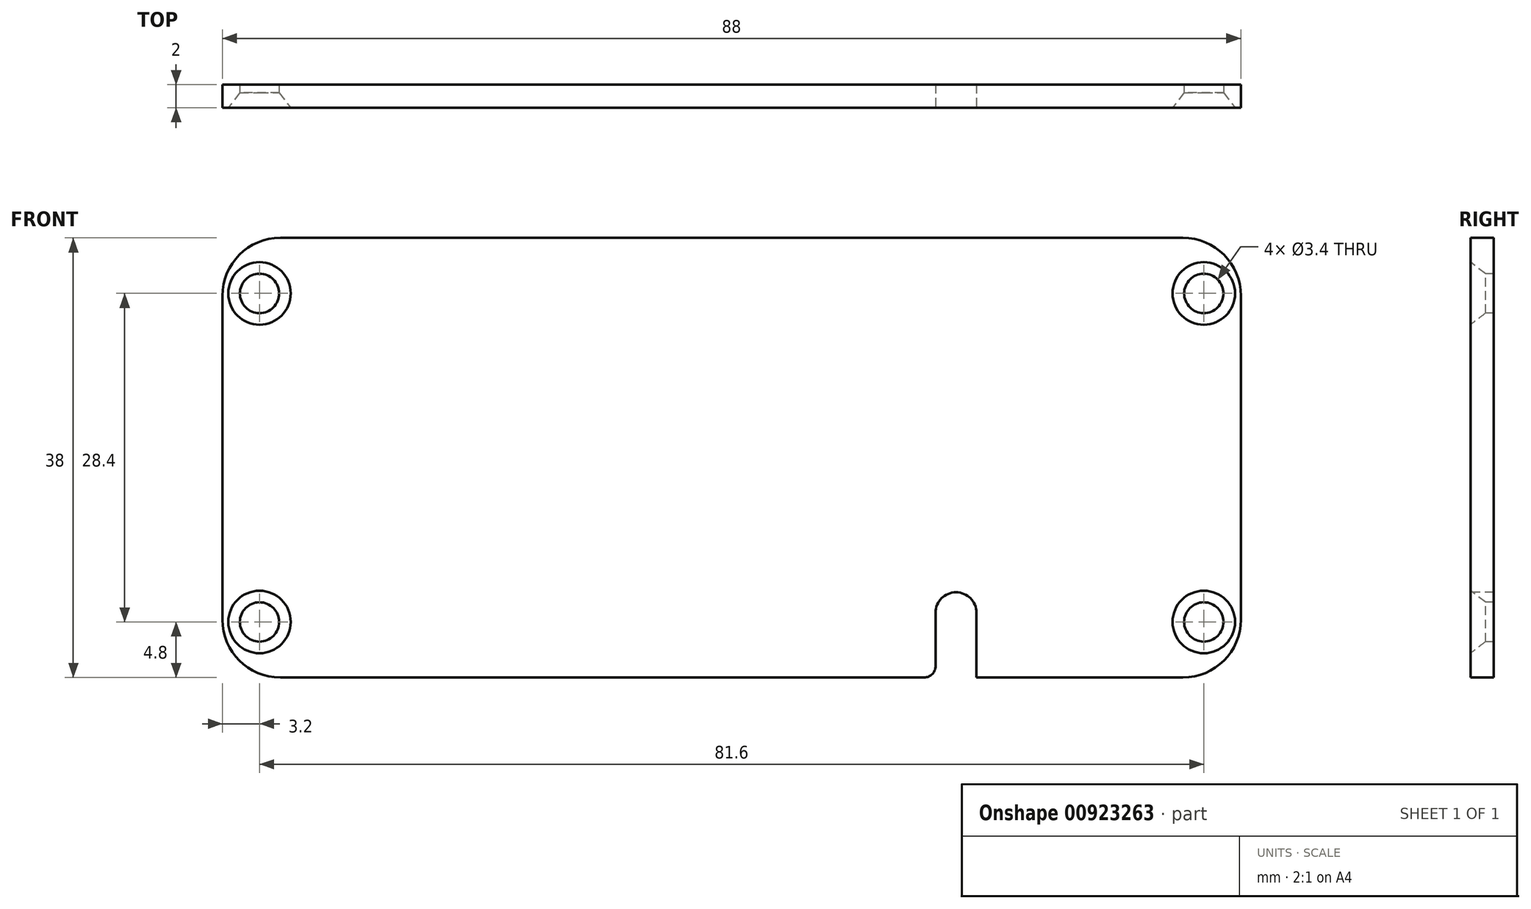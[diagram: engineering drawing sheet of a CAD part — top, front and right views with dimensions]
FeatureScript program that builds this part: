
annotation { "Feature Type Name" : "Feature", "Feature Type Description" : "" }
export const myFeature = defineFeature(function(context is Context, id is Id, definition is map)
    precondition{}
    {
        {
            var Q0;
            Q0=qCreatedBy(makeId("Front.planeOp"),FACE);
            var sketch = newSketch(context, id + "F0", { "sketchPlane" : qUnion([Q0])});
            skLineSegment(sketch, "E0.bottom", {"start": v(-88, 38) * mm, "end": v(0, 38) * mm});
            skLineSegment(sketch, "E0.top", {"start": v(-88, 0) * mm, "end": v(0, 0) * mm});
            skLineSegment(sketch, "E0.left", {"start": v(-88, 38) * mm, "end": v(-88, 0) * mm});
            skLineSegment(sketch, "E0.right", {"start": v(0, 38) * mm, "end": v(0, 0) * mm});
            skCircle(sketch, "E1", {"center": v(-84.8, 33.2) * mm, "radius": 1.7 * mm});
            skLineSegment(sketch, "E2", {"start": v(-84.8, 31.5) * mm, "end": v(-84.8, 6.5) * mm, "construction": true});
            skLineSegment(sketch, "E3", {"start": v(-84.8, 19) * mm, "end": v(0, 19) * mm, "construction": true});
            skCircle(sketch, "E4", {"center": v(-84.8, 4.8) * mm, "radius": 1.7 * mm});
            skLineSegment(sketch, "E5", {"start": v(-44, 38) * mm, "end": v(-44, 0) * mm, "construction": true});
            skCircle(sketch, "E6.MirrorC", {"center": v(-3.2, 33.2) * mm, "radius": 1.7 * mm});
            skLineSegment(sketch, "E7.MirrorCS", {"start": v(-3.2, 31.5) * mm, "end": v(-3.2, 6.5) * mm, "construction": true});
            skCircle(sketch, "E8.MirrorC", {"center": v(-3.2, 4.8) * mm, "radius": 1.7 * mm});
            skPoint(sketch, "E9.middle", {"position": v(-44, 19) * mm});
            skPoint(sketch, "E10.middle", {"position": v(-44, 7.78) * mm});
            skLineSegment(sketch, "E11", {"start": v(-26.38, 0) * mm, "end": v(-26.38, 5.6) * mm});
            skArc(sketch, "E12", {"start": v(-22.85, 5.6) * mm, "mid": v(-24.61, 7.36) * mm, "end": v(-26.38, 5.6) * mm});
            skLineSegment(sketch, "E13", {"start": v(-22.85, 5.6) * mm, "end": v(-22.85, 0) * mm});
            skSolve(sketch);
        }
        {
            var Q0;
            Q0=qSketchRegion(id+"F0",true);
            extrude(context, id + "F1", {"entities" : qUnion([Q0]), "oppositeDirection" : true, "depth" : 2 * mm, "offsetDistance" : 25 * mm});
        }
        {
            var Q0;
            Q0=makeQuery(id+"F1.opExtrude","SWEPT_EDGE",EDGE,{"disambiguationData":[OSD([sQuery(id+"F0.wireOp",EDGE,"E0.bottom"),sQuery(id+"F0.wireOp",EDGE,"E0.left")])]});
            var Q1;
            Q1=makeQuery(id+"F1.opExtrude","SWEPT_EDGE",EDGE,{"disambiguationData":[OSD([sQuery(id+"F0.wireOp",EDGE,"E0.top"),sQuery(id+"F0.wireOp",EDGE,"E0.left")])]});
            var Q2;
            Q2=makeQuery(id+"F1.opExtrude","SWEPT_EDGE",EDGE,{"disambiguationData":[OSD([sQuery(id+"F0.wireOp",EDGE,"E0.top"),sQuery(id+"F0.wireOp",EDGE,"E0.right")])]});
            var Q3;
            Q3=makeQuery(id+"F1.opExtrude","SWEPT_EDGE",EDGE,{"disambiguationData":[OSD([sQuery(id+"F0.wireOp",EDGE,"E0.bottom"),sQuery(id+"F0.wireOp",EDGE,"E0.right")])]});
            fillet(context, id + "F2", {"entities" : qUnion([Q0, Q1, Q2, Q3]), "radius" : 5 * mm, "tangentPropagation" : true, "allowEdgeOverflow" : false});
        }
        {
            var Q0;
            Q0=sQuery(id+"F0.wireOp",VERTEX,"E4.center");
            var Q1;
            Q1=sQuery(id+"F0.wireOp",VERTEX,"E1.center");
            var Q2;
            Q2=sQuery(id+"F0.wireOp",VERTEX,"E8.MirrorC.center");
            var Q3;
            Q3=sQuery(id+"F0.wireOp",VERTEX,"E6.MirrorC.center");
            var Q4;
            Q4=makeQuery(id+"F1.opExtrude","SWEPT_BODY",BODY,{"disambiguationData":[OSD([sQuery(id+"F0.wireOp",EDGE,"E0.bottom"),sQuery(id+"F0.wireOp",EDGE,"E0.top"),sQuery(id+"F0.wireOp",EDGE,"E0.left"),sQuery(id+"F0.wireOp",EDGE,"E0.right"),sQuery(id+"F0.wireOp",EDGE,"E4"),sQuery(id+"F0.wireOp",EDGE,"E1"),sQuery(id+"F0.wireOp",EDGE,"E6.MirrorC"),sQuery(id+"F0.wireOp",EDGE,"E8.MirrorC"),sQuery(id+"F0.wireOp",EDGE,"7fDMWVLP-waEW-PcbG-GO58-M4WFBlldeog6.bottom"),sQuery(id+"F0.wireOp",EDGE,"7fDMWVLP-waEW-PcbG-GO58-M4WFBlldeog6.top"),sQuery(id+"F0.wireOp",EDGE,"7fDMWVLP-waEW-PcbG-GO58-M4WFBlldeog6.left"),sQuery(id+"F0.wireOp",EDGE,"7fDMWVLP-waEW-PcbG-GO58-M4WFBlldeog6.right"),sQuery(id+"F0.wireOp",EDGE,"i3J4EDjx-qRss-jRLV-1Wwp-GzhbWhMY4lmq"),sQuery(id+"F0.wireOp",EDGE,"qa2N9Fz3-xH2k-wb9W-mJdt-cQl6CxnnNjyZ"),sQuery(id+"F0.wireOp",EDGE,"68239f5a-9685-449a-b92c-cecf612826b5"),sQuery(id+"F0.wireOp",EDGE,"E10.bottom"),sQuery(id+"F0.wireOp",EDGE,"E10.top"),sQuery(id+"F0.wireOp",EDGE,"E10.left"),sQuery(id+"F0.wireOp",EDGE,"E10.right")])]});
            hole(context, id + "F3", {"style" : HoleStyle.C_SINK, "endStyle" : HoleEndStyle.BLIND, "holeDiameter" : 3 * mm, "cSinkDiameter" : 5.4 * mm, "cSinkAngle" : 75 * degree, "majorDiameter" : 3 * mm, "holeDepth" : 13.5 * mm, "isTappedThrough" : true, "tappedDepth" : 12 * mm, "tapClearance" : 3, "locations" : qUnion([Q0, Q1, Q2, Q3]), "scope" : qUnion([Q4])});
        }
        {
            var Q0;
            {var subQ0=sQuery(id+"F0.wireOp",EDGE,"E11");Q0=makeQuery(id+"F0.imprint","IMPRINT",FACE,{"disambiguationData":[TD([[makeQuery(id+"F0.imprint","IMPRINT",EDGE,{"derivedFrom":subQ0}),-1.0]])]});}
            extrude(context, id + "F4", {"entities" : qUnion([Q0]), "operationType" : NewBodyOperationType.REMOVE, "oppositeDirection" : true, "depth" : 25 * mm, "offsetDistance" : 25 * mm});
        }
        {
            var Q0;
            Q0=makeQuery(id+"F4.boolean.opBoolean","COPY",EDGE,{"derivedFrom":makeQuery(id+"F4.opExtrude","SWEPT_EDGE",EDGE,{"disambiguationData":[OSD([sQuery(id+"F0.wireOp",EDGE,"E0.top"),sQuery(id+"F0.wireOp",EDGE,"E11")])]})});
            var Q1;
            Q1=makeQuery(id+"F4.boolean.opBoolean","COPY",EDGE,{"derivedFrom":makeQuery(id+"F4.opExtrude","SWEPT_EDGE",EDGE,{"disambiguationData":[OSD([sQuery(id+"F0.wireOp",EDGE,"E0.top"),sQuery(id+"F0.wireOp",EDGE,"E13")])]})});
            fillet(context, id + "F5", {"entities" : qUnion([Q0, Q1]), "radius" : 1 * mm, "tangentPropagation" : true, "allowEdgeOverflow" : false});
        }
    });
